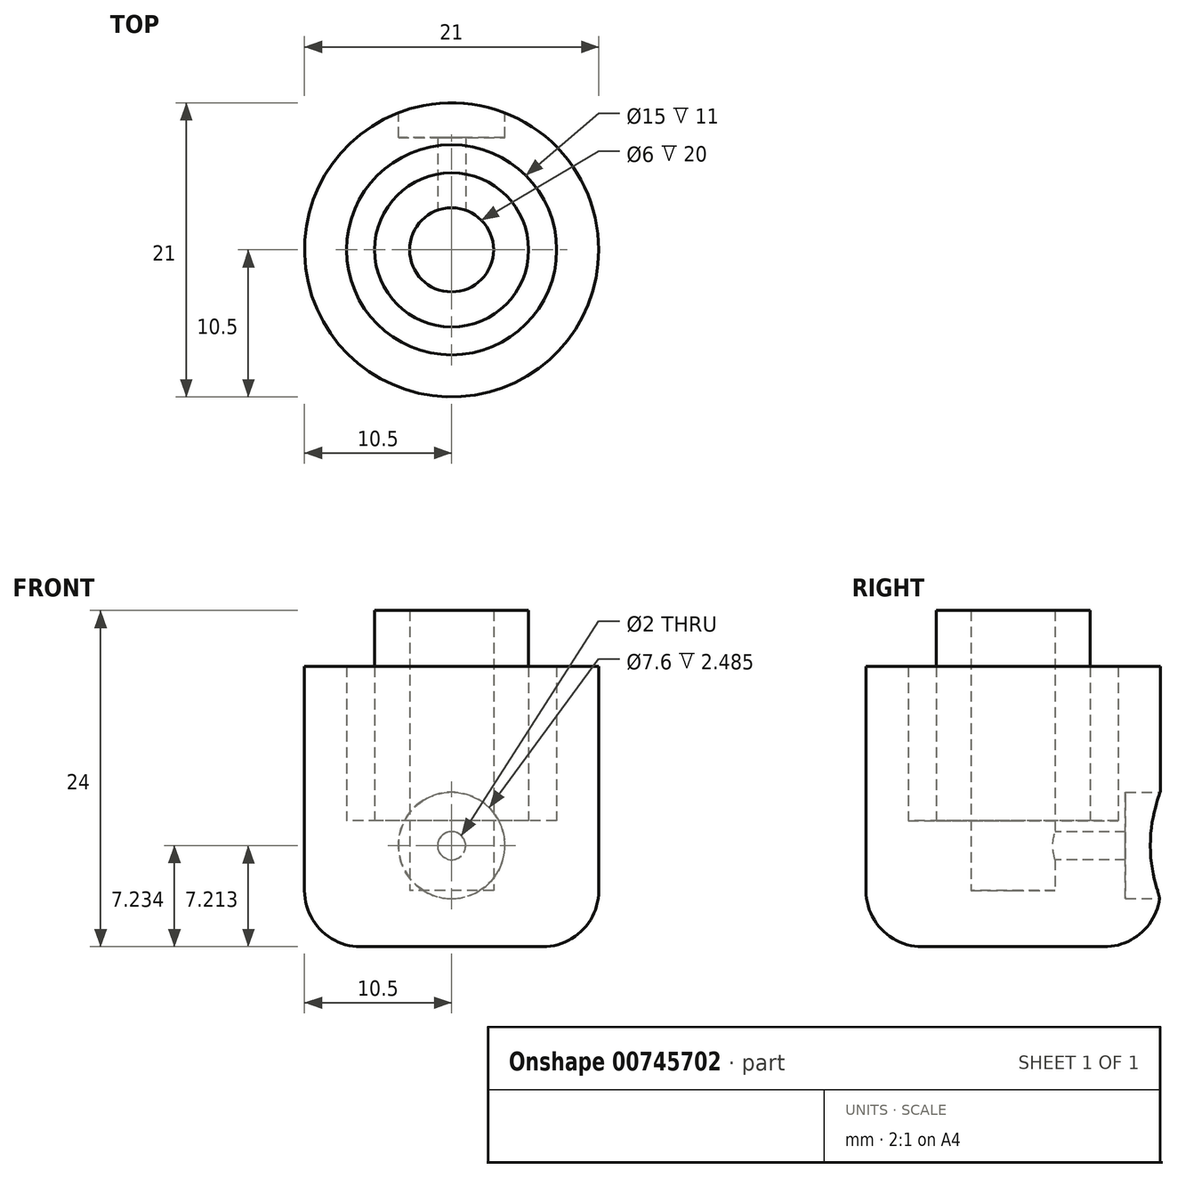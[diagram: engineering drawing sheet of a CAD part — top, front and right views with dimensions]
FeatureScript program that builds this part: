
annotation { "Feature Type Name" : "Feature", "Feature Type Description" : "" }
export const myFeature = defineFeature(function(context is Context, id is Id, definition is map)
    precondition{}
    {
        {
            var Q0;
            Q0=qCreatedBy(makeId("Top.planeOp"),FACE);
            var sketch = newSketch(context, id + "F0", { "sketchPlane" : qUnion([Q0])});
            skCircle(sketch, "E0", {"center": v(0, 0) * mm, "radius": 7.5 * mm});
            skCircle(sketch, "E1", {"center": v(0, 0) * mm, "radius": 10.5 * mm});
            skSolve(sketch);
        }
        {
            var Q0;
            Q0=makeQuery(id+"F0.imprint","IMPRINT",FACE,{"disambiguationData":[TD([[makeQuery(id+"F0.imprint","IMPRINT",EDGE,{"derivedFrom":sQuery(id+"F0.wireOp",EDGE,"E0")}),-1.0]])]});
            extrude(context, id + "F1", {"entities" : qUnion([Q0]), "depth" : 20 * mm, "offsetDistance" : 25 * mm});
        }
        {
            var Q0;
            Q0=makeQuery(id+"F0.imprint","IMPRINT",FACE,{"disambiguationData":[TD([[makeQuery(id+"F0.imprint","IMPRINT",EDGE,{"derivedFrom":sQuery(id+"F0.wireOp",EDGE,"E0")}),1.0]])]});
            extrude(context, id + "F2", {"entities" : qUnion([Q0]), "operationType" : NewBodyOperationType.ADD, "depth" : 4 * mm, "offsetDistance" : 25 * mm});
        }
        {
            var Q0;
            Q0=makeQuery(id+"F1.opExtrude","CAP_EDGE",EDGE,{"disambiguationData":[OSD([sQuery(id+"F0.wireOp",EDGE,"E1")])],"isStart":true});
            fillet(context, id + "F3", {"entities" : qUnion([Q0]), "radius" : 4 * mm, "tangentPropagation" : true, "allowEdgeOverflow" : false});
        }
        {
            var Q0;
            Q0=makeQuery(id+"F2.opExtrude","CAP_FACE",FACE,{"disambiguationData":[OSD([sQuery(id+"F0.wireOp",EDGE,"E0")])],"isStart":false});
            var sketch = newSketch(context, id + "F4", { "sketchPlane" : qUnion([Q0])});
            skCircle(sketch, "E2", {"center": v(0, 0) * mm, "radius": 5.5 * mm});
            skCircle(sketch, "E3", {"center": v(0, 0) * mm, "radius": 3 * mm});
            skSolve(sketch);
        }
        {
            var Q0;
            Q0=makeQuery(id+"F4.imprint","IMPRINT",FACE,{"disambiguationData":[TD([[makeQuery(id+"F4.imprint","IMPRINT",EDGE,{"derivedFrom":sQuery(id+"F4.wireOp",EDGE,"E2")}),1.0]])]});
            extrude(context, id + "F5", {"entities" : qUnion([Q0]), "operationType" : NewBodyOperationType.ADD, "depth" : 20 * mm, "offsetDistance" : 25 * mm});
        }
        {
            var Q0;
            {var subQ0=sQuery(id+"F0.wireOp",EDGE,"E0");Q0=makeQuery(id+"F5.boolean.opBoolean","SPLIT",FACE,{"disambiguationData":[TD([makeQuery(id+"F1.opExtrude","SWEPT_FACE",FACE,{"disambiguationData":[OSD([subQ0])]})])],"derivedFrom":makeQuery(id+"F2.opExtrude","CAP_FACE",FACE,{"disambiguationData":[OSD([subQ0])],"isStart":false})});}
            extrude(context, id + "F6", {"entities" : qUnion([Q0]), "operationType" : NewBodyOperationType.ADD, "depth" : 5 * mm, "offsetDistance" : 25 * mm});
        }
        {
            var Q0;
            Q0=qCreatedBy(makeId("Front.planeOp"),FACE);
            var sketch = newSketch(context, id + "F7", { "sketchPlane" : qUnion([Q0])});
            skCircle(sketch, "E4", {"center": v(0, 7.21) * mm, "radius": 1 * mm});
            skCircle(sketch, "E5", {"center": v(0, 7.21) * mm, "radius": 3.55 * mm});
            skSolve(sketch);
        }
        {
            var Q0;
            Q0=makeQuery(id+"F7.imprint","IMPRINT",FACE,{"disambiguationData":[TD([[makeQuery(id+"F7.imprint","IMPRINT",EDGE,{"derivedFrom":sQuery(id+"F7.wireOp",EDGE,"E4")}),1.0]])]});
            extrude(context, id + "F8", {"entities" : qUnion([Q0]), "operationType" : NewBodyOperationType.REMOVE, "oppositeDirection" : true, "depth" : 25 * mm, "offsetDistance" : 25 * mm});
        }
        {
            var Q0;
            Q0=qCreatedBy(makeId("Front.planeOp"),FACE);
            cPlane(context, id + "F9", {"entities" : qUnion([Q0]), "cplaneType" : CPlaneType.OFFSET, "offset" : 10.52 * mm, "oppositeDirection" : true, "width" : 150 * mm, "height" : 150 * mm});
        }
        {
            var Q0;
            Q0=qCreatedBy(id+"F9.planeOp",FACE);
            var sketch = newSketch(context, id + "F10", { "sketchPlane" : qUnion([Q0])});
            skCircle(sketch, "E6", {"center": v(0, 7.23) * mm, "radius": 3.8 * mm});
            skSolve(sketch);
        }
        {
            var Q0;
            Q0 = qSketchRegion(id + "F10", true);
            extrude(context, id + "F11", {"entities" : qUnion([Q0]), "operationType" : NewBodyOperationType.REMOVE, "depth" : 2.5 * mm, "offsetDistance" : 25 * mm});
        }
    });
